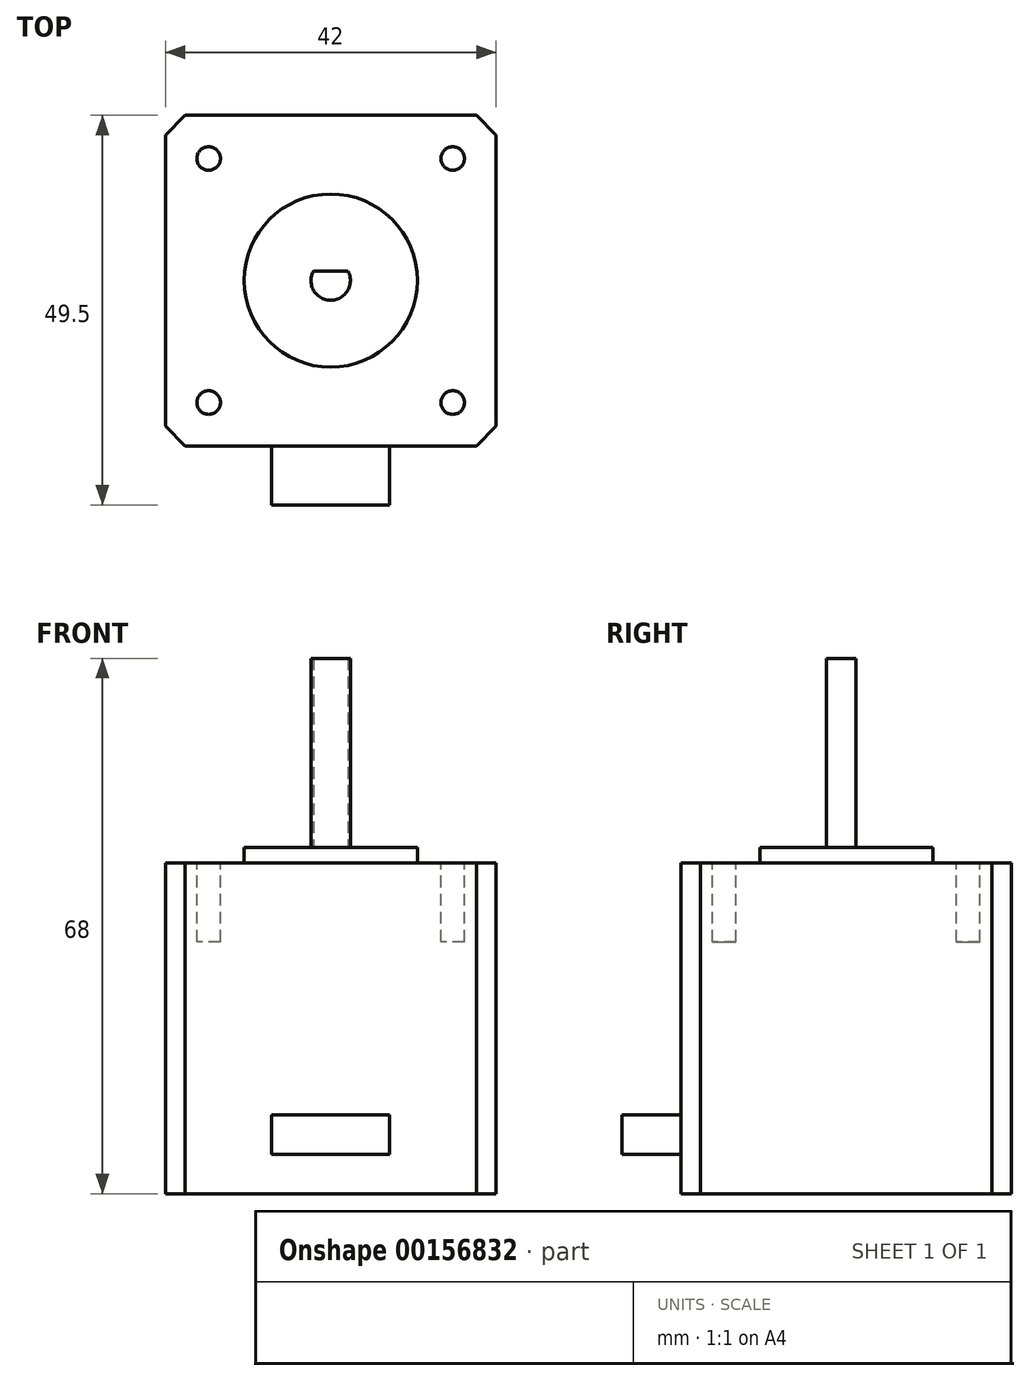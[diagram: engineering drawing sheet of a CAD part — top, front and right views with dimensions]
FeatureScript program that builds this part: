
annotation { "Feature Type Name" : "Feature", "Feature Type Description" : "" }
export const myFeature = defineFeature(function(context is Context, id is Id, definition is map)
    precondition{}
    {
        {
            var Q0;
            Q0=qCreatedBy(makeId("Top.planeOp"),FACE);
            var sketch = newSketch(context, id + "F0", { "sketchPlane" : qUnion([Q0])});
            skLineSegment(sketch, "E0.bottom", {"start": v(21, -21) * mm, "end": v(-21, -21) * mm});
            skLineSegment(sketch, "E0.top", {"start": v(21, 21) * mm, "end": v(-21, 21) * mm});
            skLineSegment(sketch, "E0.left", {"start": v(21, -21) * mm, "end": v(21, 21) * mm});
            skLineSegment(sketch, "E0.right", {"start": v(-21, -21) * mm, "end": v(-21, 21) * mm});
            skPoint(sketch, "E0.middle", {"position": v(0, 0) * mm});
            skSolve(sketch);
        }
        {
            var Q0;
            Q0=qSketchRegion(id+"F0",true);
            extrude(context, id + "F1", {"entities" : qUnion([Q0]), "depth" : 42 * mm});
        }
        {
            var Q0;
            Q0=makeQuery(id+"F1.opExtrude","SWEPT_EDGE",EDGE,{"disambiguationData":[OSD([sQuery(id+"F0.wireOp",EDGE,"E0.bottom"),sQuery(id+"F0.wireOp",EDGE,"E0.right")])]});
            var Q1;
            Q1=makeQuery(id+"F1.opExtrude","SWEPT_EDGE",EDGE,{"disambiguationData":[OSD([sQuery(id+"F0.wireOp",EDGE,"E0.bottom"),sQuery(id+"F0.wireOp",EDGE,"E0.left")])]});
            var Q2;
            Q2=makeQuery(id+"F1.opExtrude","SWEPT_EDGE",EDGE,{"disambiguationData":[OSD([sQuery(id+"F0.wireOp",EDGE,"E0.top"),sQuery(id+"F0.wireOp",EDGE,"E0.left")])]});
            var Q3;
            Q3=makeQuery(id+"F1.opExtrude","SWEPT_EDGE",EDGE,{"disambiguationData":[OSD([sQuery(id+"F0.wireOp",EDGE,"E0.top"),sQuery(id+"F0.wireOp",EDGE,"E0.right")])]});
            chamfer(context, id + "F2", {"entities" : qUnion([Q0, Q1, Q2, Q3]), "width" : 2.5 * mm, "tangentPropagation" : true});
        }
        {
            var Q0;
            Q0=makeQuery(id+"F1.opExtrude","CAP_FACE",FACE,{"disambiguationData":[OSD([sQuery(id+"F0.wireOp",EDGE,"E0.bottom"),sQuery(id+"F0.wireOp",EDGE,"E0.top"),sQuery(id+"F0.wireOp",EDGE,"E0.left"),sQuery(id+"F0.wireOp",EDGE,"E0.right")])],"isStart":false});
            var sketch = newSketch(context, id + "F3", { "sketchPlane" : qUnion([Q0])});
            skLineSegment(sketch, "E1.bottom", {"start": v(15.5, -15.5) * mm, "end": v(-15.5, -15.5) * mm, "construction": true});
            skLineSegment(sketch, "E1.top", {"start": v(15.5, 15.5) * mm, "end": v(-15.5, 15.5) * mm, "construction": true});
            skLineSegment(sketch, "E1.left", {"start": v(15.5, -15.5) * mm, "end": v(15.5, 15.5) * mm, "construction": true});
            skLineSegment(sketch, "E1.right", {"start": v(-15.5, -15.5) * mm, "end": v(-15.5, 15.5) * mm, "construction": true});
            skPoint(sketch, "E1.middle", {"position": v(0, 0) * mm});
            skCircle(sketch, "E2", {"center": v(-15.5, 15.5) * mm, "radius": 1.5 * mm});
            skCircle(sketch, "E3", {"center": v(15.5, 15.5) * mm, "radius": 1.5 * mm});
            skCircle(sketch, "E4", {"center": v(15.5, -15.5) * mm, "radius": 1.5 * mm});
            skCircle(sketch, "E5", {"center": v(-15.5, -15.5) * mm, "radius": 1.5 * mm});
            skSolve(sketch);
        }
        {
            var Q0;
            Q0=qSketchRegion(id+"F3",true);
            extrude(context, id + "F4", {"entities" : qUnion([Q0]), "operationType" : NewBodyOperationType.REMOVE, "oppositeDirection" : true, "depth" : 10 * mm});
        }
        {
            var Q0;
            Q0=makeQuery(id+"F1.opExtrude","CAP_FACE",FACE,{"disambiguationData":[OSD([sQuery(id+"F0.wireOp",EDGE,"E0.bottom"),sQuery(id+"F0.wireOp",EDGE,"E0.top"),sQuery(id+"F0.wireOp",EDGE,"E0.left"),sQuery(id+"F0.wireOp",EDGE,"E0.right")])],"isStart":false});
            var sketch = newSketch(context, id + "F5", { "sketchPlane" : qUnion([Q0])});
            skCircle(sketch, "E6", {"center": v(0, 0) * mm, "radius": 11 * mm});
            skSolve(sketch);
        }
        {
            var Q0;
            Q0=qSketchRegion(id+"F5",true);
            extrude(context, id + "F6", {"entities" : qUnion([Q0]), "operationType" : NewBodyOperationType.ADD, "depth" : 2 * mm});
        }
        {
            var Q0;
            Q0=makeQuery(id+"F6.opExtrude","CAP_FACE",FACE,{"disambiguationData":[OSD([sQuery(id+"F5.wireOp",EDGE,"E6")])],"isStart":false});
            var sketch = newSketch(context, id + "F7", { "sketchPlane" : qUnion([Q0])});
            skArc(sketch, "E7", {"start": v(-2.2, 1.2) * mm, "mid": v(0, -2.5) * mm, "end": v(2.2, 1.2) * mm});
            skLineSegment(sketch, "E8", {"start": v(-2.2, 1.2) * mm, "end": v(2.2, 1.2) * mm});
            skSolve(sketch);
        }
        {
            var Q0;
            Q0=qSketchRegion(id+"F7",true);
            extrude(context, id + "F8", {"entities" : qUnion([Q0]), "operationType" : NewBodyOperationType.ADD, "depth" : 24 * mm});
        }
        {
            var Q0;
            Q0=makeQuery(id+"F1.opExtrude","SWEPT_FACE",FACE,{"disambiguationData":[OSD([sQuery(id+"F0.wireOp",EDGE,"E0.bottom")])]});
            var sketch = newSketch(context, id + "F9", { "sketchPlane" : qUnion([Q0])});
            skLineSegment(sketch, "E9.bottom", {"start": v(7.5, 5) * mm, "end": v(-7.5, 5) * mm});
            skLineSegment(sketch, "E9.top", {"start": v(7.5, 10) * mm, "end": v(-7.5, 10) * mm});
            skLineSegment(sketch, "E9.left", {"start": v(7.5, 5) * mm, "end": v(7.5, 10) * mm});
            skLineSegment(sketch, "E9.right", {"start": v(-7.5, 5) * mm, "end": v(-7.5, 10) * mm});
            skPoint(sketch, "E9.middle", {"position": v(0, 7.5) * mm});
            skSolve(sketch);
        }
        {
            var Q0;
            Q0=qSketchRegion(id+"F9",true);
            extrude(context, id + "F10", {"entities" : qUnion([Q0]), "operationType" : NewBodyOperationType.ADD, "depth" : 7.5 * mm});
        }
    });
